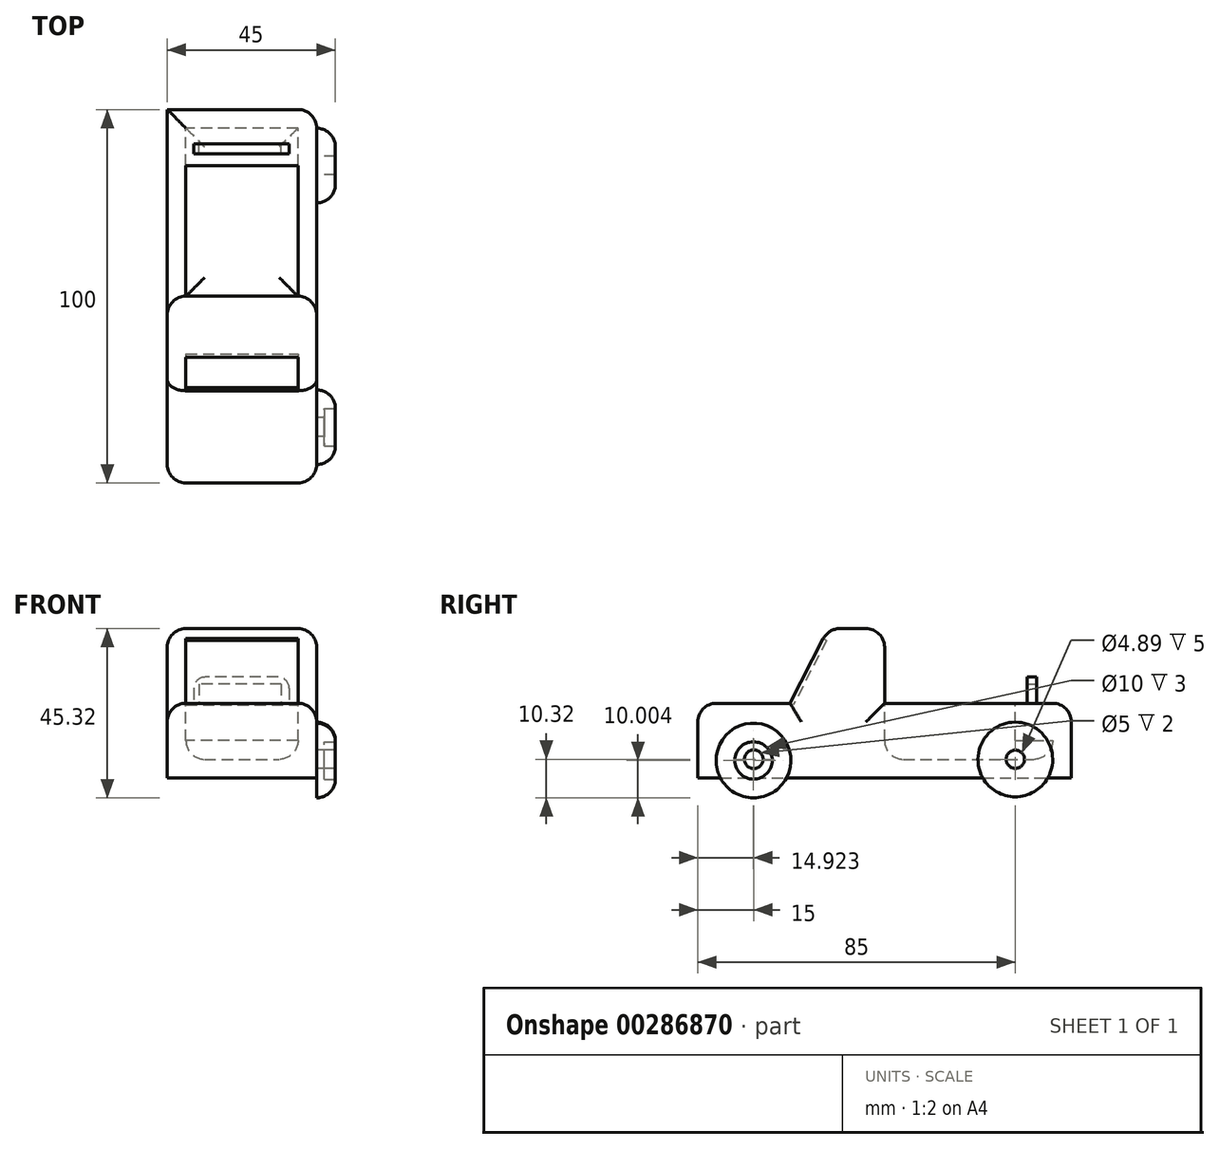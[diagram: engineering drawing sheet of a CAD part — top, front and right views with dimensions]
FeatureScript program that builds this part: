
annotation { "Feature Type Name" : "Feature", "Feature Type Description" : "" }
export const myFeature = defineFeature(function(context is Context, id is Id, definition is map)
    precondition{}
    {
        {
            var Q0;
            Q0=qCreatedBy(makeId("Right.planeOp"),FACE);
            var sketch = newSketch(context, id + "F0", { "sketchPlane" : qUnion([Q0])});
            skLineSegment(sketch, "E0.bottom", {"start": v(-50, 10) * mm, "end": v(50, 10) * mm});
            skLineSegment(sketch, "E0.top", {"start": v(-50, -10) * mm, "end": v(50, -10) * mm});
            skLineSegment(sketch, "E0.left", {"start": v(-50, 10) * mm, "end": v(-50, -10) * mm});
            skLineSegment(sketch, "E0.right", {"start": v(50, 10) * mm, "end": v(50, -10) * mm});
            skPoint(sketch, "E0.middle", {"position": v(0, 0) * mm});
            skSolve(sketch);
        }
        {
            var Q0;
            Q0=qSketchRegion(id+"F0",true);
            extrude(context, id + "F1", {"entities" : qUnion([Q0]), "depth" : 40 * mm});
        }
        {
            var Q0;
            Q0=makeQuery(id+"F1.opExtrude","CAP_FACE",FACE,{"disambiguationData":[OSD([sQuery(id+"F0.wireOp",EDGE,"E0.bottom"),sQuery(id+"F0.wireOp",EDGE,"E0.top"),sQuery(id+"F0.wireOp",EDGE,"E0.left"),sQuery(id+"F0.wireOp",EDGE,"E0.right")])],"isStart":false});
            var sketch = newSketch(context, id + "F2", { "sketchPlane" : qUnion([Q0])});
            skLineSegment(sketch, "E1", {"start": v(0, 10) * mm, "end": v(0, 30) * mm});
            skPoint(sketch, "E1.endSnap0", {"position": v(0, 10) * mm});
            skLineSegment(sketch, "E2", {"start": v(0, 30) * mm, "end": v(-15, 30) * mm});
            skLineSegment(sketch, "E3", {"start": v(-15, 30) * mm, "end": v(-25.3, 10) * mm});
            skSolve(sketch);
        }
        {
            var Q0;
            Q0=makeQuery(id+"F1.opExtrude","CAP_FACE",FACE,{"disambiguationData":[OSD([sQuery(id+"F0.wireOp",EDGE,"E0.bottom"),sQuery(id+"F0.wireOp",EDGE,"E0.top"),sQuery(id+"F0.wireOp",EDGE,"E0.left"),sQuery(id+"F0.wireOp",EDGE,"E0.right")])],"isStart":true});
            var sketch = newSketch(context, id + "F3", { "sketchPlane" : qUnion([Q0])});
            skLineSegment(sketch, "E4", {"start": v(0, 10) * mm, "end": v(0, 30) * mm});
            skPoint(sketch, "E4.endSnap0", {"position": v(0, 10) * mm});
            skLineSegment(sketch, "E5", {"start": v(0, 30) * mm, "end": v(15, 30) * mm});
            skLineSegment(sketch, "E6", {"start": v(15, 30) * mm, "end": v(25.3, 10) * mm});
            skSolve(sketch);
        }
        {
            var Q1;
            {var subQ0=sQuery(id+"F3.wireOp",EDGE,"E4");Q1=makeQuery(id+"F3.imprint","IMPRINT",FACE,{"disambiguationData":[TD([[makeQuery(id+"F3.imprint","IMPRINT",EDGE,{"derivedFrom":subQ0}),-1.0]])]});}
            var Q2;
            {var subQ0=sQuery(id+"F2.wireOp",EDGE,"E1");Q2=makeQuery(id+"F2.imprint","IMPRINT",FACE,{"disambiguationData":[TD([[makeQuery(id+"F2.imprint","IMPRINT",EDGE,{"derivedFrom":subQ0}),1.0]])]});}
            loft(context, id + "F4", {"operationType" : NewBodyOperationType.ADD, "sheetProfilesArray" : [{ "sheetProfileEntities" : qUnion([Q1]) }, { "sheetProfileEntities" : qUnion([Q2]) }]});
        }
        {
            var Q0;
            {var subQ0=sQuery(id+"F2.wireOp",EDGE,"E1");var subQ2=sQuery(id+"F0.wireOp",EDGE,"E0.bottom");Q0=makeQuery(id+"F4.boolean.opBoolean","MERGE",FACE,{"derivedFrom":[makeQuery(id+"F1.opExtrude","CAP_FACE",FACE,{"disambiguationData":[OSD([subQ2,sQuery(id+"F0.wireOp",EDGE,"E0.top"),sQuery(id+"F0.wireOp",EDGE,"E0.left"),sQuery(id+"F0.wireOp",EDGE,"E0.right")])],"isStart":false}),makeQuery(id+"F4.opLoft","CAP_FACE",FACE,{"disambiguationData":[OSD([makeQuery(id+"F2.imprint","IMPRINT",FACE,{"disambiguationData":[TD([[makeQuery(id+"F2.imprint","IMPRINT",EDGE,{"derivedFrom":subQ0}),1.0]])]})])],"isStart":true})]});}
            var sketch = newSketch(context, id + "F5", { "sketchPlane" : qUnion([Q0])});
            skCircle(sketch, "E7", {"center": v(-35, -5) * mm, "radius": 2.5 * mm});
            skCircle(sketch, "E8", {"center": v(35, -5) * mm, "radius": 2.44 * mm});
            skCircle(sketch, "E9", {"center": v(35, -5) * mm, "radius": 10 * mm});
            skCircle(sketch, "E10", {"center": v(-35, -5) * mm, "radius": 10 * mm});
            skSolve(sketch);
        }
        {
            var Q0;
            Q0=makeQuery(id+"F1.opExtrude","SWEPT_EDGE",EDGE,{"disambiguationData":[OSD([sQuery(id+"F0.wireOp",EDGE,"E0.bottom"),sQuery(id+"F0.wireOp",EDGE,"E0.left")])]});
            var Q1;
            {var subQ2=sQuery(id+"F0.wireOp",EDGE,"E0.bottom");var subQ3=sQuery(id+"F0.wireOp",EDGE,"E0.left");var subQ5=makeQuery(id+"F1.opExtrude","CAP_EDGE",EDGE,{"disambiguationData":[OSD([subQ2])],"isStart":false});Q1=makeQuery(id+"F4.boolean.opBoolean","SPLIT",EDGE,{"disambiguationData":[TD([makeQuery(id+"F1.opExtrude","SWEPT_FACE",FACE,{"disambiguationData":[OSD([subQ3])]})])],"derivedFrom":subQ5});}
            var Q2;
            {var subQ0=sQuery(id+"F0.wireOp",EDGE,"E0.right");var subQ1=sQuery(id+"F0.wireOp",EDGE,"E0.bottom");var subQ5=makeQuery(id+"F1.opExtrude","CAP_EDGE",EDGE,{"disambiguationData":[OSD([subQ1])],"isStart":false});Q2=makeQuery(id+"F4.boolean.opBoolean","SPLIT",EDGE,{"disambiguationData":[TD([makeQuery(id+"F1.opExtrude","SWEPT_FACE",FACE,{"disambiguationData":[OSD([subQ0])]})])],"derivedFrom":subQ5});}
            var Q3;
            {var subQ0=sQuery(id+"F0.wireOp",EDGE,"E0.right");var subQ1=sQuery(id+"F0.wireOp",EDGE,"E0.bottom");var subQ5=makeQuery(id+"F1.opExtrude","CAP_EDGE",EDGE,{"disambiguationData":[OSD([subQ1])],"isStart":true});Q3=makeQuery(id+"F4.boolean.opBoolean","SPLIT",EDGE,{"disambiguationData":[TD([makeQuery(id+"F1.opExtrude","SWEPT_FACE",FACE,{"disambiguationData":[OSD([subQ0])]})])],"derivedFrom":subQ5});}
            var Q4;
            {var subQ2=sQuery(id+"F0.wireOp",EDGE,"E0.bottom");var subQ3=sQuery(id+"F0.wireOp",EDGE,"E0.left");var subQ5=makeQuery(id+"F1.opExtrude","CAP_EDGE",EDGE,{"disambiguationData":[OSD([subQ2])],"isStart":true});Q4=makeQuery(id+"F4.boolean.opBoolean","SPLIT",EDGE,{"disambiguationData":[TD([makeQuery(id+"F1.opExtrude","SWEPT_FACE",FACE,{"disambiguationData":[OSD([subQ3])]})])],"derivedFrom":subQ5});}
            var Q5;
            Q5=makeQuery(id+"F1.opExtrude","SWEPT_EDGE",EDGE,{"disambiguationData":[OSD([sQuery(id+"F0.wireOp",EDGE,"E0.bottom"),sQuery(id+"F0.wireOp",EDGE,"E0.right")])]});
            var Q6;
            Q6=makeQuery(id+"F1.opExtrude","CAP_EDGE",EDGE,{"disambiguationData":[OSD([sQuery(id+"F0.wireOp",EDGE,"E0.right")])],"isStart":false});
            var Q7;
            Q7=makeQuery(id+"F1.opExtrude","CAP_EDGE",EDGE,{"disambiguationData":[OSD([sQuery(id+"F0.wireOp",EDGE,"E0.left")])],"isStart":false});
            var Q8;
            Q8=makeQuery(id+"F1.opExtrude","CAP_EDGE",EDGE,{"disambiguationData":[OSD([sQuery(id+"F0.wireOp",EDGE,"E0.left")])],"isStart":true});
            var Q9;
            Q9=makeQuery(id+"F4.opLoft","SWEPT_EDGE",EDGE,{"disambiguationData":[OSD([sQuery(id+"F2.wireOp",EDGE,"E2"),sQuery(id+"F2.wireOp",EDGE,"E3"),sQuery(id+"F3.wireOp",EDGE,"E5"),sQuery(id+"F3.wireOp",EDGE,"E6")])]});
            var Q10;
            Q10=makeQuery(id+"F4.opLoft","SWEPT_EDGE",EDGE,{"disambiguationData":[OSD([sQuery(id+"F2.wireOp",EDGE,"E1"),sQuery(id+"F2.wireOp",EDGE,"E2"),sQuery(id+"F3.wireOp",EDGE,"E4"),sQuery(id+"F3.wireOp",EDGE,"E5")])]});
            var Q11;
            Q11=makeQuery(id+"F4.opLoft","MID_CAP_EDGE",EDGE,{"disambiguationData":[OSD([sQuery(id+"F0.wireOp",EDGE,"E0.bottom"),sQuery(id+"F2.wireOp",EDGE,"E2"),sQuery(id+"F2.wireOp",EDGE,"E3")])],"capPos":1.0});
            var Q12;
            Q12=makeQuery(id+"F4.opLoft","MID_CAP_EDGE",EDGE,{"disambiguationData":[OSD([sQuery(id+"F0.wireOp",EDGE,"E0.bottom"),sQuery(id+"F2.wireOp",EDGE,"E1"),sQuery(id+"F2.wireOp",EDGE,"E2")])],"capPos":1.0});
            var Q13;
            Q13=makeQuery(id+"F4.opLoft","SWEPT_FACE",FACE,{"disambiguationData":[OSD([sQuery(id+"F2.wireOp",EDGE,"E1"),sQuery(id+"F2.wireOp",EDGE,"E2"),sQuery(id+"F2.wireOp",EDGE,"E3"),sQuery(id+"F3.wireOp",EDGE,"E4"),sQuery(id+"F3.wireOp",EDGE,"E5"),sQuery(id+"F3.wireOp",EDGE,"E6")])]});
            var Q14;
            Q14=makeQuery(id+"F4.opLoft","MID_CAP_EDGE",EDGE,{"disambiguationData":[OSD([sQuery(id+"F0.wireOp",EDGE,"E0.bottom"),sQuery(id+"F3.wireOp",EDGE,"E5"),sQuery(id+"F3.wireOp",EDGE,"E6")])],"capPos":0.0});
            var Q15;
            Q15=makeQuery(id+"F4.opLoft","MID_CAP_EDGE",EDGE,{"disambiguationData":[OSD([sQuery(id+"F0.wireOp",EDGE,"E0.bottom"),sQuery(id+"F3.wireOp",EDGE,"E4"),sQuery(id+"F3.wireOp",EDGE,"E5")])],"capPos":0.0});
            fillet(context, id + "F6", {"entities" : qUnion([Q0, Q1, Q2, Q3, Q4, Q5, Q6, Q7, Q8, Q9, Q10, Q11, Q12, Q13, Q14, Q15]), "radius" : 5 * mm, "tangentPropagation" : true, "allowEdgeOverflow" : false});
        }
        {
            var Q0;
            Q0=makeQuery(id+"F5.imprint","IMPRINT",FACE,{"disambiguationData":[TD([[makeQuery(id+"F5.imprint","IMPRINT",EDGE,{"derivedFrom":sQuery(id+"F5.wireOp",EDGE,"E7")}),1.0]])]});
            var sketch = newSketch(context, id + "F7", { "sketchPlane" : qUnion([Q0])});
            skCircle(sketch, "E11", {"center": v(-35.08, -5.32) * mm, "radius": 10 * mm});
            skSolve(sketch);
        }
        {
            var Q0;
            Q0=makeQuery(id+"F7.imprint","IMPRINT",FACE,{"disambiguationData":[TD([[makeQuery(id+"F7.imprint","IMPRINT",EDGE,{"derivedFrom":sQuery(id+"F7.wireOp",EDGE,"E11")}),1.0]])]});
            extrude(context, id + "F8", {"entities" : qUnion([Q0]), "operationType" : NewBodyOperationType.ADD, "depth" : 5 * mm});
        }
        {
            var Q0;
            Q0=makeQuery(id+"F5.imprint","IMPRINT",FACE,{"disambiguationData":[TD([[makeQuery(id+"F5.imprint","IMPRINT",EDGE,{"derivedFrom":sQuery(id+"F5.wireOp",EDGE,"E8")}),1.0]])]});
            var sketch = newSketch(context, id + "F9", { "sketchPlane" : qUnion([Q0])});
            skCircle(sketch, "E12", {"center": v(34.99, -5.05) * mm, "radius": 10 * mm});
            skSolve(sketch);
        }
        {
            var Q0;
            Q0=makeQuery(id+"F9.imprint","IMPRINT",FACE,{"disambiguationData":[TD([[makeQuery(id+"F9.imprint","IMPRINT",EDGE,{"derivedFrom":sQuery(id+"F9.wireOp",EDGE,"E12")}),1.0]])]});
            extrude(context, id + "F10", {"entities" : qUnion([Q0]), "operationType" : NewBodyOperationType.ADD, "depth" : 5 * mm});
        }
        {
            var Q0;
            Q0=makeQuery(id+"F8.opExtrude","CAP_EDGE",EDGE,{"disambiguationData":[OSD([sQuery(id+"F7.wireOp",EDGE,"E11")])],"isStart":false});
            fillet(context, id + "F11", {"entities" : qUnion([Q0]), "radius" : 5 * mm, "tangentPropagation" : true, "allowEdgeOverflow" : false});
        }
        {
            var Q0;
            Q0=makeQuery(id+"F10.opExtrude","CAP_EDGE",EDGE,{"disambiguationData":[OSD([sQuery(id+"F9.wireOp",EDGE,"E12")])],"isStart":false});
            fillet(context, id + "F12", {"entities" : qUnion([Q0]), "radius" : 5 * mm, "tangentPropagation" : true, "allowEdgeOverflow" : false});
        }
        {
            var Q0;
            {var subQ4=sQuery(id+"F0.wireOp",EDGE,"E0.bottom");var subQ5=sQuery(id+"F0.wireOp",EDGE,"E0.right");Q0=makeQuery(id+"F4.boolean.opBoolean","SPLIT",FACE,{"disambiguationData":[TD([makeQuery(id+"F1.opExtrude","SWEPT_FACE",FACE,{"disambiguationData":[OSD([subQ5])]})])],"derivedFrom":makeQuery(id+"F1.opExtrude","SWEPT_FACE",FACE,{"disambiguationData":[OSD([subQ4])]})});}
            var sketch = newSketch(context, id + "F13", { "sketchPlane" : qUnion([Q0])});
            skLineSegment(sketch, "E13.bottom", {"start": v(35, 0) * mm, "end": v(5, 0) * mm});
            skLineSegment(sketch, "E13.top", {"start": v(35, 45) * mm, "end": v(5, 45) * mm});
            skLineSegment(sketch, "E13.left", {"start": v(35, 0) * mm, "end": v(35, 45) * mm});
            skLineSegment(sketch, "E13.right", {"start": v(5, 0) * mm, "end": v(5, 45) * mm});
            skSolve(sketch);
        }
        {
            var Q0;
            Q0=makeQuery(id+"F13.imprint","IMPRINT",FACE,{"disambiguationData":[TD([[makeQuery(id+"F13.imprint","IMPRINT",EDGE,{"derivedFrom":sQuery(id+"F13.wireOp",EDGE,"E13.bottom")}),1.0]])]});
            extrude(context, id + "F14", {"entities" : qUnion([Q0]), "operationType" : NewBodyOperationType.REMOVE, "oppositeDirection" : true, "depth" : 15 * mm});
        }
        {
            var Q0;
            Q0=makeQuery(id+"F14.boolean.opBoolean","COPY",EDGE,{"derivedFrom":makeQuery(id+"F14.opExtrude","CAP_EDGE",EDGE,{"disambiguationData":[OSD([sQuery(id+"F13.wireOp",EDGE,"E13.bottom")])],"isStart":false})});
            var Q1;
            Q1=makeQuery(id+"F14.boolean.opBoolean","COPY",EDGE,{"derivedFrom":makeQuery(id+"F14.opExtrude","CAP_EDGE",EDGE,{"disambiguationData":[OSD([sQuery(id+"F13.wireOp",EDGE,"E13.right")])],"isStart":false})});
            var Q2;
            Q2=makeQuery(id+"F14.boolean.opBoolean","COPY",EDGE,{"derivedFrom":makeQuery(id+"F14.opExtrude","CAP_EDGE",EDGE,{"disambiguationData":[OSD([sQuery(id+"F13.wireOp",EDGE,"E13.top")])],"isStart":false})});
            var Q3;
            Q3=makeQuery(id+"F14.boolean.opBoolean","COPY",EDGE,{"derivedFrom":makeQuery(id+"F14.opExtrude","CAP_EDGE",EDGE,{"disambiguationData":[OSD([sQuery(id+"F13.wireOp",EDGE,"E13.left")])],"isStart":false})});
            fillet(context, id + "F15", {"entities" : qUnion([Q0, Q1, Q2, Q3]), "radius" : 5 * mm, "tangentPropagation" : true, "allowEdgeOverflow" : false});
        }
        {
            var Q0;
            Q0=makeQuery(id+"F4.opLoft","SWEPT_FACE",FACE,{"disambiguationData":[OSD([sQuery(id+"F0.wireOp",EDGE,"E0.bottom"),sQuery(id+"F2.wireOp",EDGE,"E2"),sQuery(id+"F2.wireOp",EDGE,"E3"),sQuery(id+"F3.wireOp",EDGE,"E5"),sQuery(id+"F3.wireOp",EDGE,"E6")])]});
            extrude(context, id + "F16", {"entities" : qUnion([Q0]), "operationType" : NewBodyOperationType.REMOVE, "oppositeDirection" : true, "depth" : 1 * mm});
        }
        {
            var Q0;
            Q0=makeQuery(id+"F8.opExtrude","CAP_FACE",FACE,{"disambiguationData":[OSD([sQuery(id+"F5.wireOp",EDGE,"E7"),sQuery(id+"F7.wireOp",EDGE,"E11")])],"isStart":false});
            extrude(context, id + "F17", {"entities" : qUnion([Q0]), "operationType" : NewBodyOperationType.REMOVE, "oppositeDirection" : true, "depth" : 3 * mm});
        }
        {
            var Q0;
            Q0=makeQuery(id+"F14.boolean.opBoolean","COPY",FACE,{"derivedFrom":makeQuery(id+"F14.opExtrude","SWEPT_FACE",FACE,{"disambiguationData":[OSD([sQuery(id+"F13.wireOp",EDGE,"E13.top")])]})});
            extrude(context, id + "F18", {"entities" : qUnion([Q0]), "operationType" : NewBodyOperationType.ADD, "depth" : 10 * mm});
        }
        {
            var Q0;
            Q0=makeQuery(id+"F18.opExtrude","SWEPT_FACE",FACE,{"disambiguationData":[OSD([sQuery(id+"F0.wireOp",EDGE,"E0.bottom"),sQuery(id+"F0.wireOp",EDGE,"E0.right"),sQuery(id+"F13.wireOp",EDGE,"E13.top")])]});
            var sketch = newSketch(context, id + "F19", { "sketchPlane" : qUnion([Q0])});
            skLineSegment(sketch, "E14.bottom", {"start": v(32.64, 38.17) * mm, "end": v(7.16, 38.17) * mm});
            skLineSegment(sketch, "E14.top", {"start": v(32.64, 40.74) * mm, "end": v(7.16, 40.74) * mm});
            skLineSegment(sketch, "E14.left", {"start": v(32.64, 38.17) * mm, "end": v(32.64, 40.74) * mm});
            skLineSegment(sketch, "E14.right", {"start": v(7.16, 38.17) * mm, "end": v(7.16, 40.74) * mm});
            skSolve(sketch);
        }
        {
            var Q0;
            Q0=makeQuery(id+"F19.imprint","IMPRINT",FACE,{"disambiguationData":[TD([[makeQuery(id+"F19.imprint","IMPRINT",EDGE,{"derivedFrom":sQuery(id+"F19.wireOp",EDGE,"E14.bottom")}),-1.0]])]});
            extrude(context, id + "F20", {"entities" : qUnion([Q0]), "operationType" : NewBodyOperationType.ADD, "depth" : 7 * mm});
        }
        {
            var Q0;
            Q0=makeQuery(id+"F20.opExtrude","SWEPT_FACE",FACE,{"disambiguationData":[OSD([sQuery(id+"F19.wireOp",EDGE,"E14.top")])]});
            var sketch = newSketch(context, id + "F21", { "sketchPlane" : qUnion([Q0])});
            skLineSegment(sketch, "E15.bottom", {"start": v(-30.53, 15.1) * mm, "end": v(-8.55, 15.1) * mm});
            skLineSegment(sketch, "E15.top", {"start": v(-30.53, 10) * mm, "end": v(-8.55, 10) * mm});
            skLineSegment(sketch, "E15.left", {"start": v(-30.53, 15.1) * mm, "end": v(-30.53, 10) * mm});
            skLineSegment(sketch, "E15.right", {"start": v(-8.55, 15.1) * mm, "end": v(-8.55, 10) * mm});
            skSolve(sketch);
        }
        {
            var Q0;
            Q0=makeQuery(id+"F21.imprint","IMPRINT",FACE,{"disambiguationData":[TD([[makeQuery(id+"F21.imprint","IMPRINT",EDGE,{"derivedFrom":sQuery(id+"F21.wireOp",EDGE,"E15.bottom")}),-1.0]])]});
            extrude(context, id + "F22", {"entities" : qUnion([Q0]), "operationType" : NewBodyOperationType.REMOVE, "oppositeDirection" : true, "depth" : 25 * mm});
        }
        {
            var Q0;
            Q0=makeQuery(id+"F20.opExtrude","CAP_EDGE",EDGE,{"disambiguationData":[OSD([sQuery(id+"F19.wireOp",EDGE,"E14.left")])],"isStart":false});
            var Q1;
            Q1=makeQuery(id+"F20.opExtrude","CAP_EDGE",EDGE,{"disambiguationData":[OSD([sQuery(id+"F19.wireOp",EDGE,"E14.right")])],"isStart":false});
            fillet(context, id + "F23", {"entities" : qUnion([Q0, Q1]), "radius" : 3 * mm, "tangentPropagation" : true, "allowEdgeOverflow" : false});
        }
    });
